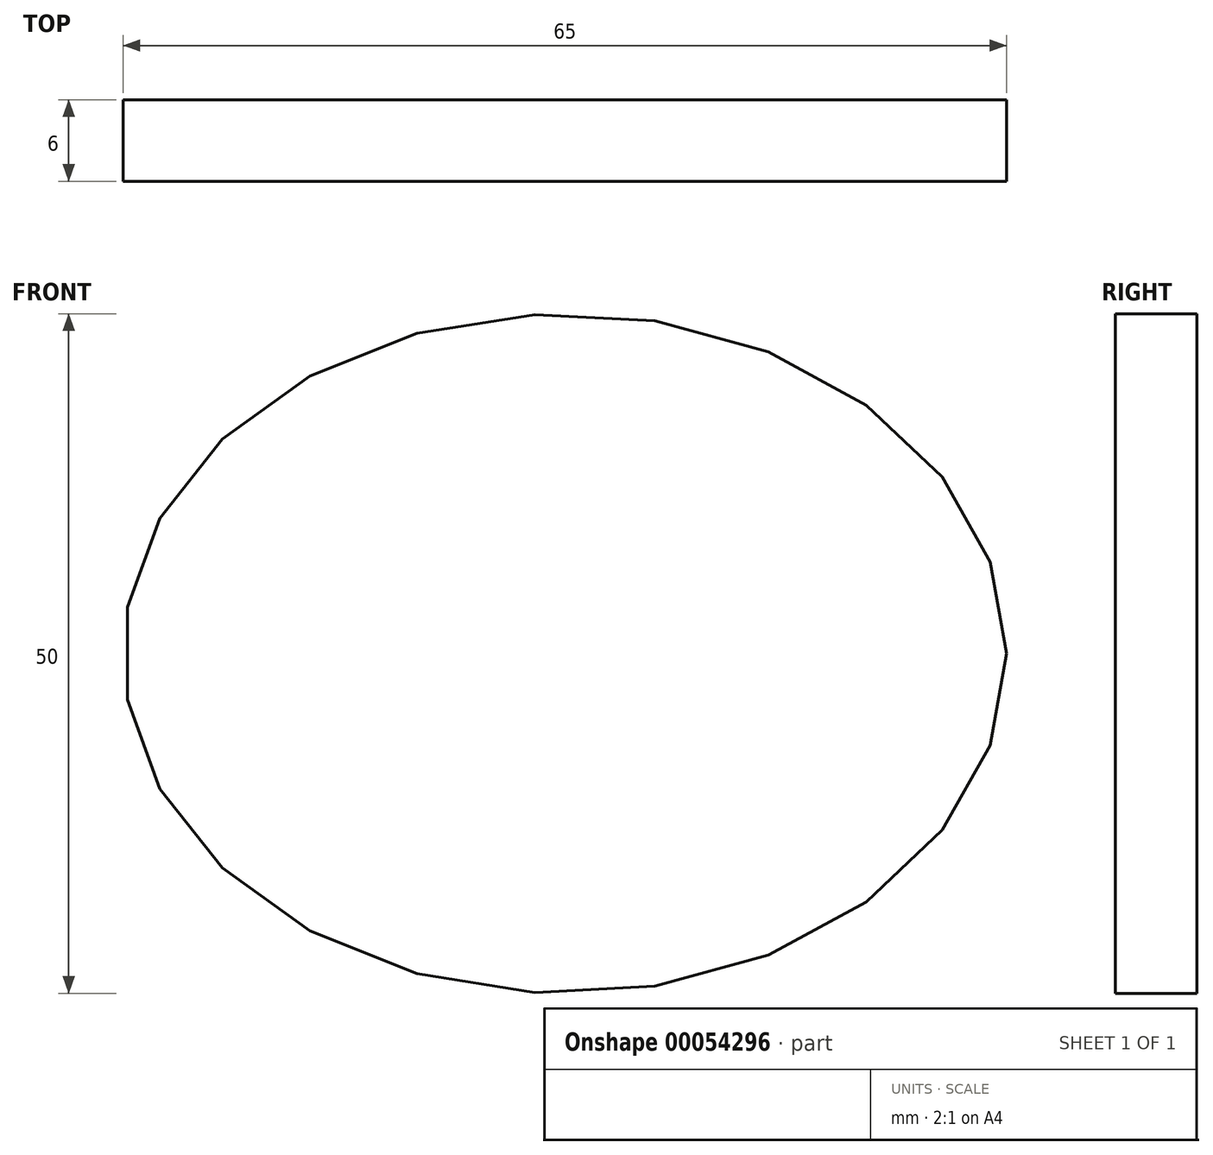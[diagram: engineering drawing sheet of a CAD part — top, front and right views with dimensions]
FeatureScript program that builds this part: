
annotation { "Feature Type Name" : "Feature", "Feature Type Description" : "" }
export const myFeature = defineFeature(function(context is Context, id is Id, definition is map)
    precondition{}
    {
        {
            var Q0;
            Q0=qCreatedBy(makeId("Front.planeOp"),FACE);
            var sketch = newSketch(context, id + "F0", { "sketchPlane" : qUnion([Q0])});
            skEllipse(sketch, "E0", {"center": v(0, 0) * mm, "majorRadius": 32.5 * mm, "minorRadius": 25 * mm, "majorAxis": v(1, 0)});
            skFitSpline(sketch, "E1.0", {"points": [v(35.47, -1.43) * mm, v(35.52, 0) * mm, v(35.47, 1.43) * mm, v(35.29, 3.33) * mm, v(34.83, 5.67) * mm, v(33.94, 8.4) * mm, v(32.72, 11) * mm, v(31.19, 13.5) * mm, v(29.35, 15.86) * mm, v(27.6, 17.7) * mm, v(26.05, 19.07) * mm, v(24.82, 20.06) * mm, v(23.54, 21) * mm, v(21.76, 22.18) * mm, v(19.43, 23.5) * mm, v(16.47, 24.87) * mm, v(13.37, 26) * mm, v(10.15, 26.88) * mm, v(6.84, 27.52) * mm, v(4.01, 27.85) * mm, v(1.73, 27.98) * mm, v(0, 28.01) * mm, v(-1.73, 27.98) * mm, v(-4.01, 27.85) * mm, v(-6.84, 27.52) * mm, v(-10.15, 26.88) * mm, v(-13.37, 26) * mm, v(-16.47, 24.87) * mm, v(-19.43, 23.5) * mm, v(-21.76, 22.18) * mm, v(-23.54, 21) * mm, v(-24.82, 20.06) * mm, v(-26.05, 19.07) * mm, v(-27.6, 17.7) * mm, v(-29.35, 15.86) * mm, v(-31.19, 13.5) * mm, v(-32.72, 11) * mm, v(-33.94, 8.4) * mm, v(-34.83, 5.67) * mm, v(-35.29, 3.33) * mm, v(-35.47, 1.43) * mm, v(-35.52, 0) * mm, v(-35.47, -1.43) * mm, v(-35.29, -3.33) * mm, v(-34.83, -5.67) * mm, v(-33.94, -8.4) * mm, v(-32.72, -11) * mm, v(-31.19, -13.5) * mm, v(-29.35, -15.86) * mm, v(-27.6, -17.7) * mm, v(-26.05, -19.07) * mm, v(-24.82, -20.06) * mm, v(-23.54, -21) * mm, v(-21.76, -22.18) * mm, v(-19.43, -23.5) * mm, v(-16.47, -24.87) * mm, v(-13.37, -26) * mm, v(-10.15, -26.88) * mm, v(-6.84, -27.52) * mm, v(-4.01, -27.85) * mm, v(-1.73, -27.98) * mm, v(0, -28.01) * mm, v(1.73, -27.98) * mm, v(4.01, -27.85) * mm, v(6.84, -27.52) * mm, v(10.15, -26.88) * mm, v(13.37, -26) * mm, v(16.47, -24.87) * mm, v(19.43, -23.5) * mm, v(21.76, -22.18) * mm, v(23.54, -21) * mm, v(24.82, -20.06) * mm, v(26.05, -19.07) * mm, v(27.6, -17.7) * mm, v(29.35, -15.86) * mm, v(31.19, -13.5) * mm, v(32.72, -11) * mm, v(33.94, -8.4) * mm, v(34.83, -5.67) * mm, v(35.29, -3.33) * mm, v(35.47, -1.43) * mm, v(35.52, 0) * mm, v(35.47, 1.43) * mm, v(35.47, -1.43) * mm]});
            skSolve(sketch);
        }
        {
            var Q0;
            Q0 = qSketchRegion(id + "F0", true);
            extrude(context, id + "F1", {"entities" : qUnion([Q0]), "depth" : 6 * mm});
        }
    });
